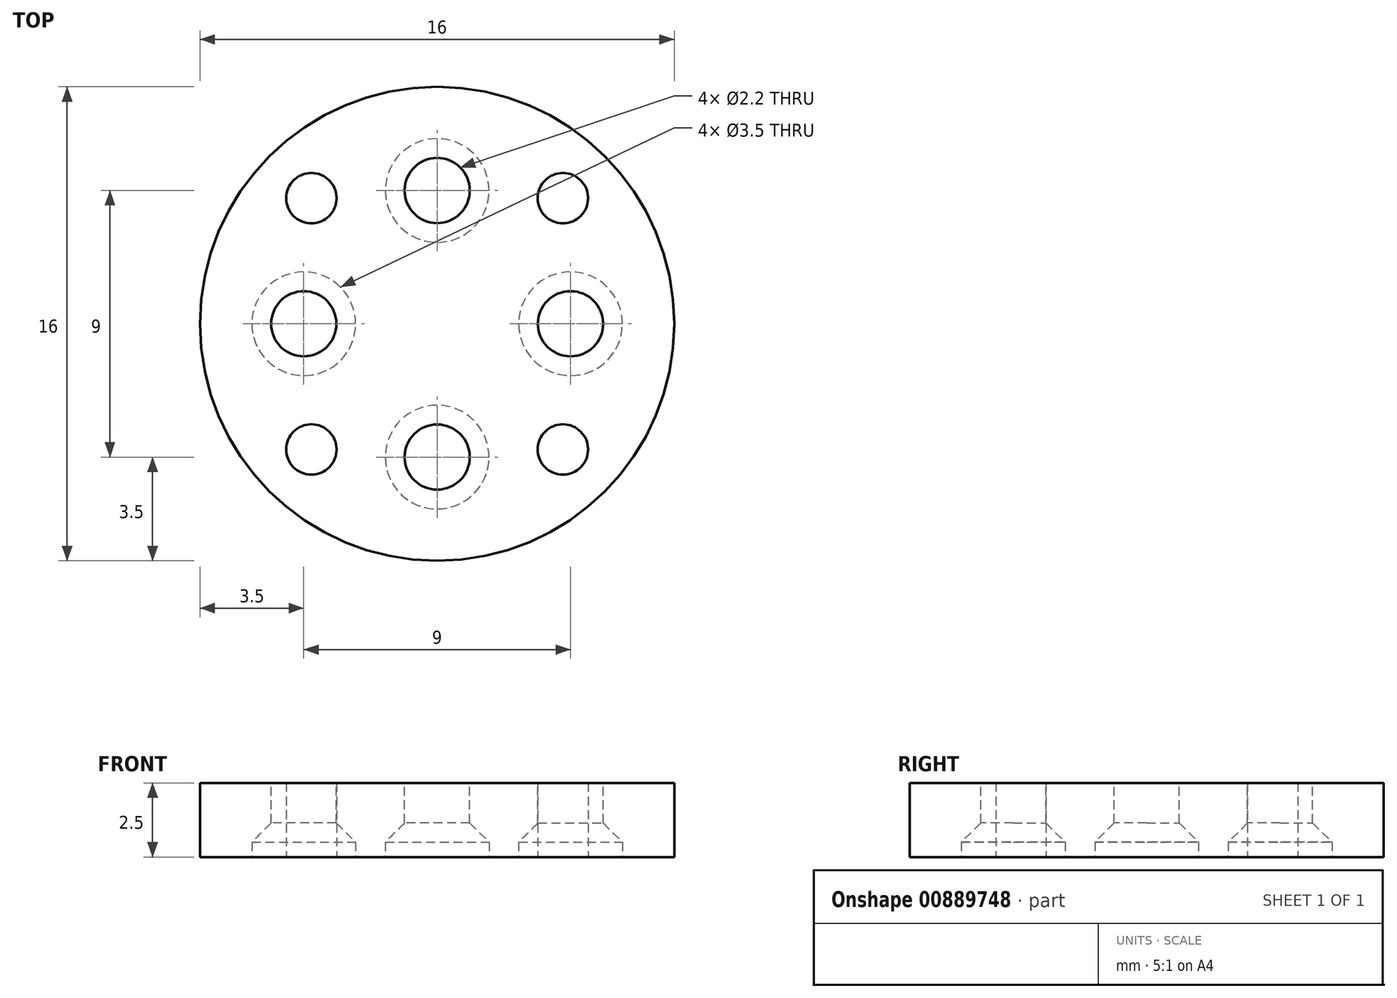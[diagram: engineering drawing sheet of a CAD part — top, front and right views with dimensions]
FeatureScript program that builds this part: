
annotation { "Feature Type Name" : "Feature", "Feature Type Description" : "" }
export const myFeature = defineFeature(function(context is Context, id is Id, definition is map)
    precondition{}
    {
        {
            var Q0;
            Q0=qCreatedBy(makeId("Top.planeOp"),FACE);
            var sketch = newSketch(context, id + "F0", { "sketchPlane" : qUnion([Q0])});
            skCircle(sketch, "E0", {"center": v(0, 0) * mm, "radius": 8 * mm});
            skSolve(sketch);
        }
        {
            var Q0;
            Q0=makeQuery(id+"F0.imprint","IMPRINT",FACE,{"disambiguationData":[TD([[makeQuery(id+"F0.imprint","IMPRINT",EDGE,{"derivedFrom":sQuery(id+"F0.wireOp",EDGE,"E0")}),1.0]])]});
            extrude(context, id + "F1", {"entities" : qUnion([Q0]), "depth" : 2.5 * mm});
        }
        {
            var Q0;
            Q0=makeQuery(id+"F1.opExtrude","CAP_FACE",FACE,{"disambiguationData":[OSD([sQuery(id+"F0.wireOp",EDGE,"E0")])],"isStart":false});
            var sketch = newSketch(context, id + "F2", { "sketchPlane" : qUnion([Q0])});
            skCircle(sketch, "E1", {"center": v(0, 4.5) * mm, "radius": 1.1 * mm});
            skCircle(sketch, "E2.1.0", {"center": v(-4.5, 0) * mm, "radius": 1.1 * mm});
            skCircle(sketch, "E2.2.0", {"center": v(0, -4.5) * mm, "radius": 1.1 * mm});
            skCircle(sketch, "E2.3.0", {"center": v(4.5, 0) * mm, "radius": 1.1 * mm});
            skPoint(sketch, "E2.center", {"position": v(0, 0) * mm});
            skSolve(sketch);
        }
        {
            var Q0;
            Q0=qSketchRegion(id+"F2",true);
            extrude(context, id + "F3", {"entities" : qUnion([Q0]), "operationType" : NewBodyOperationType.REMOVE, "endBound" : BoundingType.THROUGH_ALL, "oppositeDirection" : true, "depth" : 25 * mm});
        }
        {
            var Q0;
            Q0=makeQuery(id+"F1.opExtrude","CAP_FACE",FACE,{"disambiguationData":[OSD([sQuery(id+"F0.wireOp",EDGE,"E0")])],"isStart":true});
            var sketch = newSketch(context, id + "F4", { "sketchPlane" : qUnion([Q0])});
            skCircle(sketch, "E3", {"center": v(4.24, 4.24) * mm, "radius": 0.85 * mm});
            skCircle(sketch, "E4.1.0", {"center": v(-4.24, 4.24) * mm, "radius": 0.85 * mm});
            skCircle(sketch, "E4.2.0", {"center": v(-4.24, -4.24) * mm, "radius": 0.85 * mm});
            skCircle(sketch, "E4.3.0", {"center": v(4.24, -4.24) * mm, "radius": 0.85 * mm});
            skPoint(sketch, "E4.center", {"position": v(0, 0) * mm});
            skLineSegment(sketch, "E5", {"start": v(0, 0) * mm, "end": v(4.24, 4.24) * mm, "construction": true});
            skSolve(sketch);
        }
        {
            var Q0;
            Q0=makeQuery(id+"F4.imprint","IMPRINT",FACE,{"disambiguationData":[TD([[makeQuery(id+"F4.imprint","IMPRINT",EDGE,{"derivedFrom":sQuery(id+"F4.wireOp",EDGE,"E4.1.0")}),1.0]])]});
            var Q1;
            Q1=makeQuery(id+"F4.imprint","IMPRINT",FACE,{"disambiguationData":[TD([[makeQuery(id+"F4.imprint","IMPRINT",EDGE,{"derivedFrom":sQuery(id+"F4.wireOp",EDGE,"E3")}),1.0]])]});
            var Q2;
            Q2=makeQuery(id+"F4.imprint","IMPRINT",FACE,{"disambiguationData":[TD([[makeQuery(id+"F4.imprint","IMPRINT",EDGE,{"derivedFrom":sQuery(id+"F4.wireOp",EDGE,"E4.3.0")}),1.0]])]});
            var Q3;
            Q3=makeQuery(id+"F4.imprint","IMPRINT",FACE,{"disambiguationData":[TD([[makeQuery(id+"F4.imprint","IMPRINT",EDGE,{"derivedFrom":sQuery(id+"F4.wireOp",EDGE,"E4.2.0")}),1.0]])]});
            extrude(context, id + "F5", {"entities" : qUnion([Q0, Q1, Q2, Q3]), "operationType" : NewBodyOperationType.REMOVE, "endBound" : BoundingType.THROUGH_ALL, "oppositeDirection" : true, "depth" : 25 * mm});
        }
        {
            var Q0;
            Q0=makeQuery(id+"F1.opExtrude","CAP_FACE",FACE,{"disambiguationData":[OSD([sQuery(id+"F0.wireOp",EDGE,"E0")])],"isStart":false});
            var sketch = newSketch(context, id + "F6", { "sketchPlane" : qUnion([Q0])});
            skArc(sketch, "E6", {"start": v(-4.24, 2.4) * mm, "mid": v(-2.93, 2.93) * mm, "end": v(-2.4, 4.24) * mm});
            skLineSegment(sketch, "E7", {"start": v(-2.4, 7.63) * mm, "end": v(-2.4, 4.24) * mm});
            skLineSegment(sketch, "E8", {"start": v(-7.63, 2.4) * mm, "end": v(-4.24, 2.4) * mm});
            skLineSegment(sketch, "E9", {"start": v(-4.24, 4.24) * mm, "end": v(0, 0) * mm, "construction": true});
            skArc(sketch, "E10.0", {"start": v(-2.4, 7.63) * mm, "mid": v(-5.66, 5.66) * mm, "end": v(-7.63, 2.4) * mm});
            skLineSegment(sketch, "E11.1.0", {"start": v(-2.4, -7.63) * mm, "end": v(-2.4, -4.24) * mm});
            skArc(sketch, "E11.1.1", {"start": v(-7.63, -2.4) * mm, "mid": v(-5.66, -5.66) * mm, "end": v(-2.4, -7.63) * mm});
            skLineSegment(sketch, "E11.1.2", {"start": v(-7.63, -2.4) * mm, "end": v(-4.24, -2.4) * mm});
            skArc(sketch, "E11.1.3", {"start": v(-2.4, -4.24) * mm, "mid": v(-2.93, -2.93) * mm, "end": v(-4.24, -2.4) * mm});
            skLineSegment(sketch, "E11.2.0", {"start": v(7.63, -2.4) * mm, "end": v(4.24, -2.4) * mm});
            skArc(sketch, "E11.2.1", {"start": v(2.4, -7.63) * mm, "mid": v(5.66, -5.66) * mm, "end": v(7.63, -2.4) * mm});
            skLineSegment(sketch, "E11.2.2", {"start": v(2.4, -7.63) * mm, "end": v(2.4, -4.24) * mm});
            skArc(sketch, "E11.2.3", {"start": v(4.24, -2.4) * mm, "mid": v(2.93, -2.93) * mm, "end": v(2.4, -4.24) * mm});
            skLineSegment(sketch, "E11.3.0", {"start": v(2.4, 7.63) * mm, "end": v(2.4, 4.24) * mm});
            skArc(sketch, "E11.3.1", {"start": v(7.63, 2.4) * mm, "mid": v(5.66, 5.66) * mm, "end": v(2.4, 7.63) * mm});
            skLineSegment(sketch, "E11.3.2", {"start": v(7.63, 2.4) * mm, "end": v(4.24, 2.4) * mm});
            skArc(sketch, "E11.3.3", {"start": v(2.4, 4.24) * mm, "mid": v(2.93, 2.93) * mm, "end": v(4.24, 2.4) * mm});
            skSolve(sketch);
        }
        {
            var Q0;
            Q0=qCreatedBy(makeId("Top.planeOp"),FACE);
            var sketch = newSketch(context, id + "F7", { "sketchPlane" : qUnion([Q0])});
            skCircle(sketch, "E12", {"center": v(0, -4.5) * mm, "radius": 1.75 * mm});
            skCircle(sketch, "E13", {"center": v(0, 4.5) * mm, "radius": 1.75 * mm});
            skCircle(sketch, "E14", {"center": v(-4.5, 0) * mm, "radius": 1.75 * mm});
            skCircle(sketch, "E15", {"center": v(4.5, 0) * mm, "radius": 1.75 * mm});
            skSolve(sketch);
        }
        {
            var Q0;
            Q0=qSketchRegion(id+"F7",true);
            extrude(context, id + "F8", {"entities" : qUnion([Q0]), "operationType" : NewBodyOperationType.REMOVE, "depth" : 0.5 * mm});
        }
        {
            var Q0;
            Q0=makeQuery(id+"F8.boolean.opBoolean","COPY",FACE,{"derivedFrom":makeQuery(id+"F8.opExtrude","CAP_FACE",FACE,{"disambiguationData":[OSD([sQuery(id+"F7.wireOp",EDGE,"E15")])],"isStart":false})});
            var sketch = newSketch(context, id + "F9", { "sketchPlane" : qUnion([Q0])});
            skCircle(sketch, "E16.0", {"center": v(0, 4.5) * mm, "radius": 1.75 * mm});
            skCircle(sketch, "E17.0", {"center": v(-4.5, 0) * mm, "radius": 1.75 * mm});
            skCircle(sketch, "E18.0", {"center": v(0, -4.5) * mm, "radius": 1.75 * mm});
            skCircle(sketch, "E19.0", {"center": v(4.5, 0) * mm, "radius": 1.75 * mm});
            skSolve(sketch);
        }
        {
            var Q0;
            Q0=qSketchRegion(id+"F9",true);
            extrude(context, id + "F10", {"entities" : qUnion([Q0]), "operationType" : NewBodyOperationType.REMOVE, "oppositeDirection" : true, "depth" : 25 * mm, "hasDraft" : true, "draftAngle" : 45 * degree, "draftPullDirection" : true});
        }
    });
